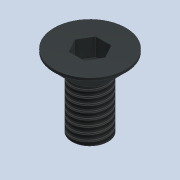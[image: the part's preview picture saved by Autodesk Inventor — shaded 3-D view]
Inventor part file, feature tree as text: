
AUTODESK INVENTOR PART (.ipt)
format: ipt  version: 2020.4 (Build 244396000, 396)  size: 165,888 bytes
history: native  units: mm
features: extrude x3, sketch x3, other x1, chamfer x1, thread x1
ambient origin geometry x8: Origin, YZ Plane, XZ Plane, XY Plane, X Axis, Y Axis, Z Axis, Center Point
bodies: Body1 (feature_tree)
feature tree (9):
  other  "ソリッド1"
  extrude  "押し出し1"  Depth=4.0mm
  extrude  "押し出し2"  Depth=5.7mm TaperAngle=0.0deg
  chamfer  "面取り1"  Distance=8.0mm
  extrude  "押し出し3"  Depth=2.3mm TaperAngle=0.0deg
  thread  "ねじ1"
  sketch  "スケッチ1"
  sketch  "スケッチ2"
  sketch  "スケッチ3"
